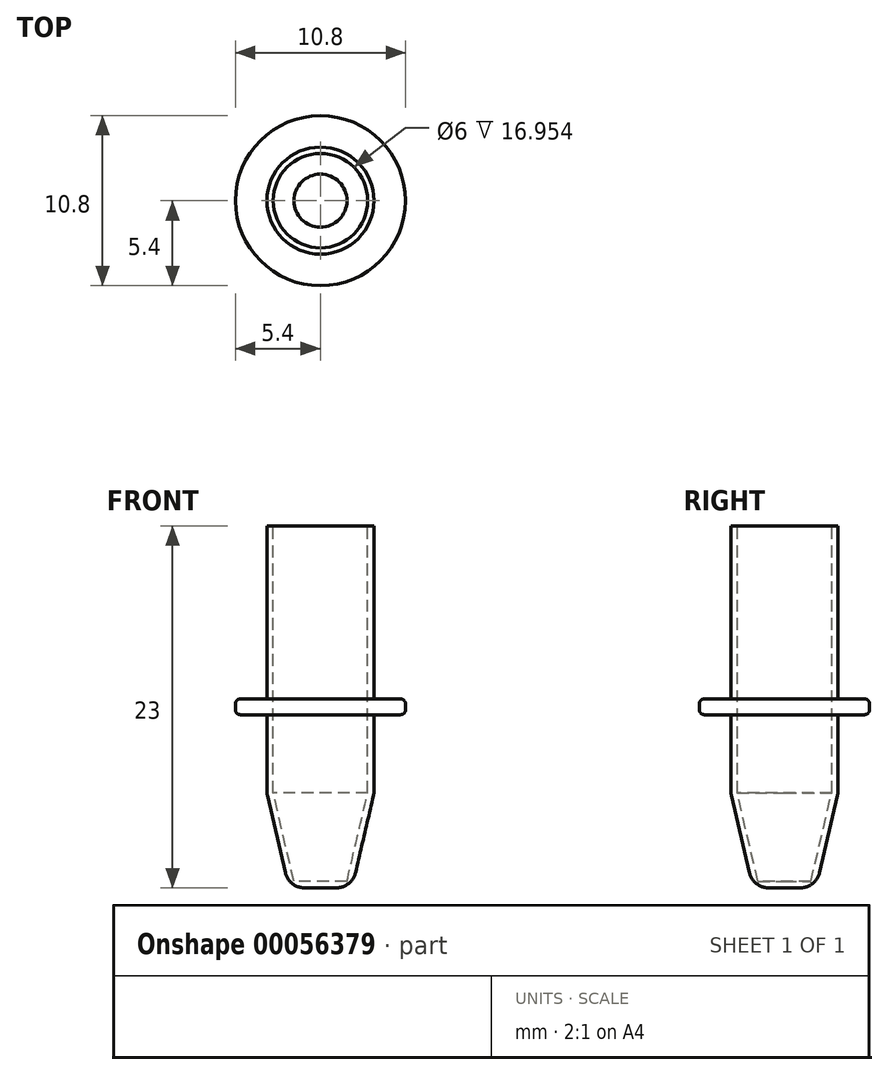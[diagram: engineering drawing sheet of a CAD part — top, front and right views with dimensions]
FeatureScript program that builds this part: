
annotation { "Feature Type Name" : "Feature", "Feature Type Description" : "" }
export const myFeature = defineFeature(function(context is Context, id is Id, definition is map)
    precondition{}
    {
        {
            var Q0;
            Q0=qCreatedBy(makeId("Front.planeOp"),FACE);
            var sketch = newSketch(context, id + "F0", { "sketchPlane" : qUnion([Q0])});
            skLineSegment(sketch, "E0", {"start": v(0, 0) * mm, "end": v(3, 0) * mm, "construction": true});
            skLineSegment(sketch, "E1", {"start": v(3, 0) * mm, "end": v(3.4, 0) * mm, "construction": true});
            skLineSegment(sketch, "E2", {"start": v(0, 0) * mm, "end": v(0, -23) * mm, "construction": true});
            skLineSegment(sketch, "E3", {"start": v(0, -23) * mm, "end": v(2, -23) * mm});
            skLineSegment(sketch, "E4", {"start": v(3, 0) * mm, "end": v(3, -16.95) * mm});
            skLineSegment(sketch, "E5", {"start": v(3, 0) * mm, "end": v(3.4, 0) * mm});
            skLineSegment(sketch, "E6", {"start": v(3.4, 0) * mm, "end": v(3.4, -11) * mm});
            skLineSegment(sketch, "E7", {"start": v(3.4, -11) * mm, "end": v(5.4, -11) * mm});
            skLineSegment(sketch, "E8", {"start": v(5.4, -11) * mm, "end": v(5.4, -12) * mm});
            skLineSegment(sketch, "E9", {"start": v(5.4, -12) * mm, "end": v(3.4, -12) * mm});
            skLineSegment(sketch, "E10", {"start": v(3.4, -12) * mm, "end": v(3.4, -17) * mm});
            skLineSegment(sketch, "E11", {"start": v(3.4, -17) * mm, "end": v(2, -23) * mm});
            skLineSegment(sketch, "E12", {"start": v(0, -23) * mm, "end": v(0, -22.6) * mm});
            skLineSegment(sketch, "E13", {"start": v(0, -22.6) * mm, "end": v(1.68, -22.6) * mm});
            skLineSegment(sketch, "E14", {"start": v(1.68, -22.6) * mm, "end": v(3, -16.95) * mm});
            skSolve(sketch);
        }
        {
            var Q0;
            Q0=makeQuery(id+"F0.imprint","IMPRINT",FACE,{"disambiguationData":[TD([[makeQuery(id+"F0.imprint","IMPRINT",EDGE,{"derivedFrom":sQuery(id+"F0.wireOp",EDGE,"E3")}),1.0]])]});
            var Q1;
            Q1=sQuery(id+"F0.wireOp",EDGE,"E2");
            revolve(context, id + "F1", {"entities" : qUnion([Q0]), "axis" : qUnion([Q1]), "revolveType" : RevolveType.FULL});
        }
        {
            var Q0;
            Q0=makeQuery(id+"F1.opRevolve","SWEPT_EDGE",EDGE,{"disambiguationData":[OSD([sQuery(id+"F0.wireOp",EDGE,"E3"),sQuery(id+"F0.wireOp",EDGE,"E11")])]});
            var Q1;
            Q1=makeQuery(id+"F1.opRevolve","SWEPT_EDGE",EDGE,{"disambiguationData":[OSD([sQuery(id+"F0.wireOp",EDGE,"E10"),sQuery(id+"F0.wireOp",EDGE,"E11")])]});
            fillet(context, id + "F2", {"entities" : qUnion([Q0, Q1]), "radius" : 1.25 * mm, "tangentPropagation" : true, "allowEdgeOverflow" : false});
        }
        {
            var Q0;
            Q0=makeQuery(id+"F1.opRevolve","SWEPT_EDGE",EDGE,{"disambiguationData":[OSD([sQuery(id+"F0.wireOp",EDGE,"E7"),sQuery(id+"F0.wireOp",EDGE,"E8")])]});
            var Q1;
            Q1=makeQuery(id+"F1.opRevolve","SWEPT_EDGE",EDGE,{"disambiguationData":[OSD([sQuery(id+"F0.wireOp",EDGE,"E8"),sQuery(id+"F0.wireOp",EDGE,"E9")])]});
            fillet(context, id + "F3", {"entities" : qUnion([Q0, Q1]), "radius" : 0.3 * mm, "tangentPropagation" : true, "allowEdgeOverflow" : false});
        }
    });
